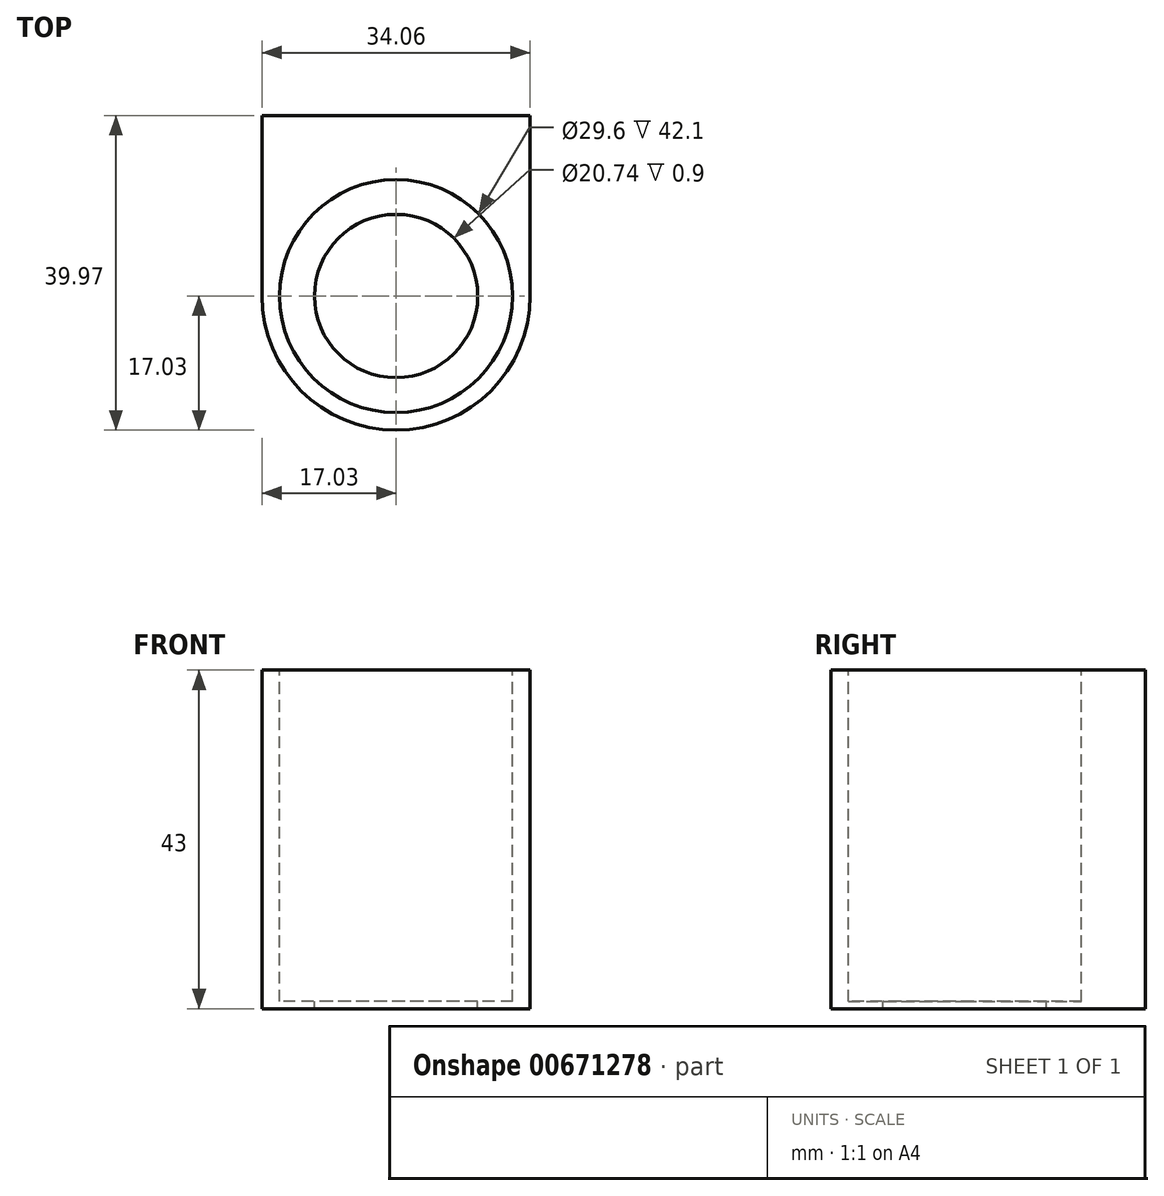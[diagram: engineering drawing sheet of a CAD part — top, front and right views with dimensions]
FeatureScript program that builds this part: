
annotation { "Feature Type Name" : "Feature", "Feature Type Description" : "" }
export const myFeature = defineFeature(function(context is Context, id is Id, definition is map)
    precondition{}
    {
        {
            var Q0;
            Q0=qCreatedBy(makeId("Top.planeOp"),FACE);
            var sketch = newSketch(context, id + "F0", { "sketchPlane" : qUnion([Q0])});
            skLineSegment(sketch, "E0.bottom", {"start": v(17.03, 0) * mm, "end": v(17.03, 0) * mm});
            skLineSegment(sketch, "E0.top", {"start": v(17.03, 22.94) * mm, "end": v(-17.03, 22.94) * mm});
            skLineSegment(sketch, "E0.left", {"start": v(17.03, 0) * mm, "end": v(17.03, 22.94) * mm});
            skLineSegment(sketch, "E0.right", {"start": v(-17.03, 0) * mm, "end": v(-17.03, 22.94) * mm});
            skLineSegment(sketch, "E1", {"start": v(-17.03, 0) * mm, "end": v(-17.03, 0) * mm});
            skArc(sketch, "E2", {"start": v(17.03, 0) * mm, "mid": v(0, 17.03) * mm, "end": v(-17.03, 0) * mm, "construction": true});
            skArc(sketch, "E3", {"start": v(-17.03, 0) * mm, "mid": v(0, -17.03) * mm, "end": v(17.03, 0) * mm});
            skLineSegment(sketch, "E4", {"start": v(17.03, 0) * mm, "end": v(-17.03, 0) * mm, "construction": true});
            skSolve(sketch);
        }
        {
            var Q0;
            Q0 = qSketchRegion(id + "F0", true);
            var Q1;
            Q1 = qConstructionFilter(qBodyType(qCreatedBy(id + "F0" ,EDGE), BodyType.WIRE), ConstructionObject.NO);
            extrude(context, id + "F1", {"entities" : qUnion([Q0]), "surfaceEntities" : qUnion([Q1]), "depth" : 43 * mm, "offsetDistance" : 25 * mm});
        }
        {
            var Q0;
            Q0=makeQuery(id+"F1.opExtrude","CAP_FACE",FACE,{"disambiguationData":[OSD([sQuery(id+"F0.wireOp",EDGE,"E0.top"),sQuery(id+"F0.wireOp",EDGE,"E0.left"),sQuery(id+"F0.wireOp",EDGE,"E0.right"),sQuery(id+"F0.wireOp",EDGE,"E3")])],"isStart":false});
            var sketch = newSketch(context, id + "F2", { "sketchPlane" : qUnion([Q0])});
            skCircle(sketch, "E5", {"center": v(0, 0) * mm, "radius": 14.8 * mm});
            skSolve(sketch);
        }
        {
            var Q0;
            Q0=makeQuery(id+"F2.imprint","IMPRINT",FACE,{"disambiguationData":[TD([[makeQuery(id+"F2.imprint","IMPRINT",EDGE,{"derivedFrom":sQuery(id+"F2.wireOp",EDGE,"E5")}),-1.0]])]});
            var sketch = newSketch(context, id + "F3", { "sketchPlane" : qUnion([Q0])});
            skCircle(sketch, "E6", {"center": v(0, 0) * mm, "radius": 10.37 * mm});
            skSolve(sketch);
        }
        {
            var Q0;
            Q0 = qSketchRegion(id + "F2", true);
            extrude(context, id + "F4", {"entities" : qUnion([Q0]), "operationType" : NewBodyOperationType.REMOVE, "oppositeDirection" : true, "depth" : 42.1 * mm, "offsetDistance" : 25 * mm});
        }
        {
            var Q0;
            Q0 = qSketchRegion(id + "F3", true);
            extrude(context, id + "F5", {"entities" : qUnion([Q0]), "operationType" : NewBodyOperationType.REMOVE, "endBound" : BoundingType.THROUGH_ALL, "oppositeDirection" : true, "depth" : 25 * mm, "offsetDistance" : 25 * mm});
        }
    });
